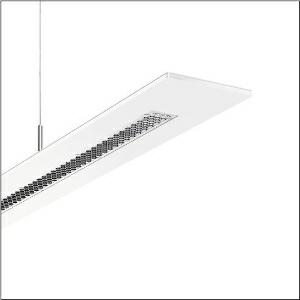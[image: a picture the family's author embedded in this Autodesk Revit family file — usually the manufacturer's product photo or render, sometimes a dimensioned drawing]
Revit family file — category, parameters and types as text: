
# Revit family: arktika_r__21_duo_5mb252dl60840_f6f7
name_source: partatom
category: Lighting Fixtures
units: mm (PartAtom-declared; Revit-internal decimal feet)

## family parameters
Cut with Voids When Loaded = No
Host = Face
Light Source = No
Part Type = Normal
Room Calculation Point = No
Round Connector Dimension = Use Diameter
Shared = No

## types (1)
- --- (1 x LED 4000K / CRI = 80 (unbekannt), 8800 lm, 4000K)
    Apparent Load = 67 VA
    CIE Flux Codes = 81 100 100 79 100
    Color Rendering = 80
    Color Temperature = 4000K
    Default Elevation = 1800 mm
    Description = Arktika® 21, office luminaire, primary anti-glare with honeycomb louvre, of plastic, aluminium vaporised, highly specular, light emission: direct/indirect distribution, primary light characteristic: symmetric, installation type: suspended mounting, LED rated luminous flux: 8.800 lm, light colour: 840, colour temperature: 4000K, control gear: ECG DALI, with terminal, 3+2-pole, max. 2.5mm², mains connection: 220..240V, AC, 50/60Hz, rated input power: 67W, housing, of aluminium, powder-coated, traffic white (RAL 9016), 2-length, length: 2.280 mm, width: 120 mm, height: 8mm, protection rating (complete): IP20, insulation class (complete): insulation class II (safety insulation), certification: CE, packaging unit: 1 piece
    Height = 8 mm  [stored 0.0262467 ft]
    Lamp = 1 x LED 4000K / CRI >= 80 (unbekannt)
    Lamp Light Flux = 8800 lm
    Lamp count = 1
    Length = 2280 mm
    Luminous efficacy = 132 lm/W
    Manufacturer = Siteco
    ModVariant = No
    Model = 5MB252DL60840
    Mounting Place = Ceiling
    Mounting Type = Pendant
    Number of Poles = 1
    OnlyDefault = Yes
    Power Factor = 1
    Product Name = Arktika® 21 duo
    Product group = office luminaire | ceiling pendant
    ProductGroupID = 905
    Protection Class = Protection class II
    Protection Degree = IP 20
    RLX_Detail_Level = 1
    RlxData = <blob elided: 39737 chars, md5=d19aa2e4>
    Socket = socket
    Standby Power = 0 W
    System Light Flux = 8800 lm
    System Power = 67 W
    Type Comments = factory setting: luminous flux: 100 % | dim-lin: 254 | 1330 mA
    Type Image = l_1006128.jpg
    URL = http://relux.com
    VarID = @adj_145793
    Voltage = 0 V
    Weight = 0.00 kg
    Width = 120 mm

note: [stored X ft] marks values corroborated as IEEE doubles in the binary element streams (Revit-internal decimal feet)

## geometry (parser evidence)
native form markers: Blend x4, Sweep x12
no freeform markers — native parametric forms only
